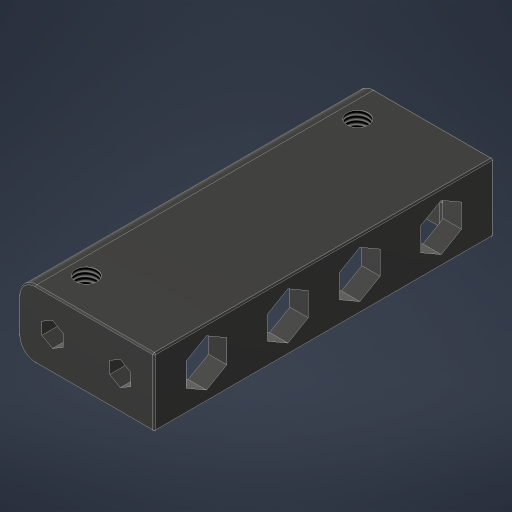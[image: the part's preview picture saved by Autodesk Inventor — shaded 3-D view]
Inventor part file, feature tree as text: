
AUTODESK INVENTOR PART (.ipt)
format: ipt  version: 2023.4 (Build 274418000, 418)  size: 367,104 bytes
history: native  units: in
note: dims shown in document units (in); Inventor stores cm internally (conversion verified against a paired STEP export)
features: sketch x5, extrude x4, fillet x3, projected_geometry x2, hole x1
ambient origin geometry x8: Origin, YZ Plane, XZ Plane, XY Plane, X Axis, Y Axis, Z Axis, Center Point
bodies: Solid1 (feature_tree)
feature tree (15):
  extrude  "Extrusion1"  Depth=0.5in
  hole  "Hole1"  [1 undecoded]
  fillet  "Fillet1"  Radius=0.25in
  fillet  "Fillet2"  Radius=0.125in
  extrude  "Extrusion2"  Depth=0.125in
  fillet  "Fillet3"  Radius=0.125in
  extrude  "Extrusion3"  Depth=0.375in TaperAngle=0.0deg
  extrude  "Extrusion4"  Depth=0.13in
  sketch  "Sketch1"  dims[d0=1.0in d1=0.5in]
  sketch  "Sketch2"  dims[d2=2.5in d3=0.0in d4=2.0in d5=0.25in]
  sketch  "Sketch3"  dims[d6=0.156in d7=0.38in d8=0.385in d9=0.25in d10=0.5635in d11=1.0in d12=0.8108in d13=0.125in]
  sketch  "Sketch4"  dims[d14=0.01in d15=0.125in d16=0.125in]
  sketch  "Sketch5"  dims[d17=0.125in d18=0.375in d19=0.0in d20=0.13in d21=0.3in d22=0.375in d23=0.7874in d25=0.6in d26=0.3937in d28=1.0in d30=0.0in d31=0.0in d32=0.25in d33=0.0in d34=0.0in]
  projected_geometry  "Project Cut Edges1"
  projected_geometry  "Project Cut Edges2"
note: 1 required parameter value undecoded (feature->parameter linkage not recoverable at this tier; creation-order binding heuristic only, values carry confidence <= 0.55)
